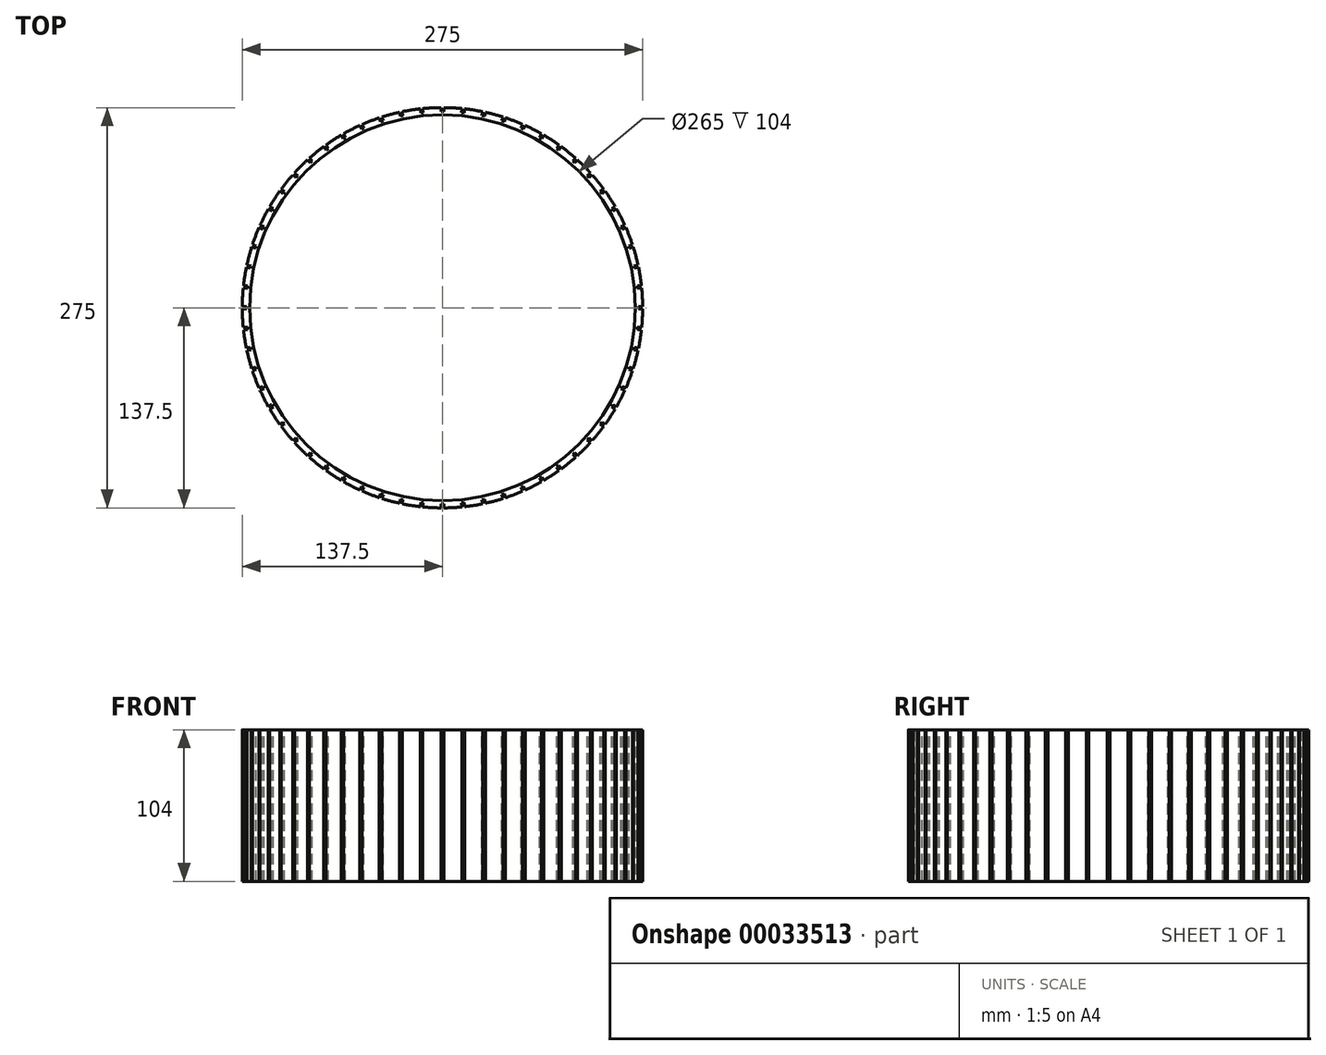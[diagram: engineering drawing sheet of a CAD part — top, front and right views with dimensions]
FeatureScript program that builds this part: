
annotation { "Feature Type Name" : "Feature", "Feature Type Description" : "" }
export const myFeature = defineFeature(function(context is Context, id is Id, definition is map)
    precondition{}
    {
        {
            var Q0;
            Q0=qCreatedBy(makeId("Top.planeOp"),FACE);
            var sketch = newSketch(context, id + "F0", { "sketchPlane" : qUnion([Q0])});
            skCircle(sketch, "E0", {"center": v(0, 0) * mm, "radius": 137.5 * mm});
            skCircle(sketch, "E1", {"center": v(0, 0) * mm, "radius": 132.5 * mm});
            skSolve(sketch);
        }
        {
            var Q0;
            Q0=makeQuery(id+"F0.imprint","IMPRINT",FACE,{"disambiguationData":[TD([[makeQuery(id+"F0.imprint","IMPRINT",EDGE,{"derivedFrom":sQuery(id+"F0.wireOp",EDGE,"E0")}),1.0]])]});
            extrude(context, id + "F1", {"entities" : qUnion([Q0]), "depth" : 104 * mm});
        }
        {
            var Q0;
            Q0=makeQuery(id+"F1.opExtrude","CAP_FACE",FACE,{"disambiguationData":[OSD([sQuery(id+"F0.wireOp",EDGE,"E0"),sQuery(id+"F0.wireOp",EDGE,"E1")])],"isStart":false});
            var sketch = newSketch(context, id + "F2", { "sketchPlane" : qUnion([Q0])});
            skCircle(sketch, "E2", {"center": v(0, 0) * mm, "radius": 134.7 * mm, "construction": true});
            skLineSegment(sketch, "E3", {"start": v(0, 0) * mm, "end": v(0, -137.5) * mm, "construction": true});
            skLineSegment(sketch, "E4.rect.bottom", {"start": v(0.9, -140.3) * mm, "end": v(-0.9, -140.3) * mm});
            skLineSegment(sketch, "E4.rect.top", {"start": v(0.9, -134.7) * mm, "end": v(-0.9, -134.7) * mm});
            skLineSegment(sketch, "E4.rect.left", {"start": v(0.9, -140.3) * mm, "end": v(0.9, -134.7) * mm});
            skLineSegment(sketch, "E4.rect.right", {"start": v(-0.9, -140.3) * mm, "end": v(-0.9, -134.7) * mm});
            skPoint(sketch, "E4.rect.middle", {"position": v(0, -137.5) * mm});
            skLineSegment(sketch, "E5.1.0", {"start": v(13.77, -139.63) * mm, "end": v(13.18, -134.06) * mm});
            skLineSegment(sketch, "E5.1.1", {"start": v(15.56, -139.44) * mm, "end": v(13.77, -139.63) * mm});
            skLineSegment(sketch, "E5.1.2", {"start": v(15.56, -139.44) * mm, "end": v(14.98, -133.87) * mm});
            skLineSegment(sketch, "E5.1.3", {"start": v(14.98, -133.87) * mm, "end": v(13.18, -134.06) * mm});
            skLineSegment(sketch, "E5.2.0", {"start": v(28.29, -137.42) * mm, "end": v(27.13, -131.94) * mm});
            skLineSegment(sketch, "E5.2.1", {"start": v(30.05, -137.05) * mm, "end": v(28.29, -137.42) * mm});
            skLineSegment(sketch, "E5.2.2", {"start": v(30.05, -137.05) * mm, "end": v(28.89, -131.57) * mm});
            skLineSegment(sketch, "E5.2.3", {"start": v(28.89, -131.57) * mm, "end": v(27.13, -131.94) * mm});
            skLineSegment(sketch, "E5.3.0", {"start": v(42.5, -133.71) * mm, "end": v(40.77, -128.39) * mm});
            skLineSegment(sketch, "E5.3.1", {"start": v(44.21, -133.16) * mm, "end": v(42.5, -133.71) * mm});
            skLineSegment(sketch, "E5.3.2", {"start": v(44.21, -133.16) * mm, "end": v(42.48, -127.83) * mm});
            skLineSegment(sketch, "E5.3.3", {"start": v(42.48, -127.83) * mm, "end": v(40.77, -128.39) * mm});
            skLineSegment(sketch, "E5.4.0", {"start": v(56.24, -128.54) * mm, "end": v(53.97, -123.42) * mm});
            skLineSegment(sketch, "E5.4.1", {"start": v(57.89, -127.8) * mm, "end": v(56.24, -128.54) * mm});
            skLineSegment(sketch, "E5.4.2", {"start": v(57.89, -127.8) * mm, "end": v(55.6, -122.69) * mm});
            skLineSegment(sketch, "E5.4.3", {"start": v(55.6, -122.69) * mm, "end": v(53.97, -123.42) * mm});
            skLineSegment(sketch, "E5.5.0", {"start": v(69.37, -121.95) * mm, "end": v(66.57, -117.1) * mm});
            skLineSegment(sketch, "E5.5.1", {"start": v(70.93, -121.05) * mm, "end": v(69.37, -121.95) * mm});
            skLineSegment(sketch, "E5.5.2", {"start": v(70.93, -121.05) * mm, "end": v(68.13, -116.2) * mm});
            skLineSegment(sketch, "E5.5.3", {"start": v(68.13, -116.2) * mm, "end": v(66.57, -117.1) * mm});
            skLineSegment(sketch, "E5.6.0", {"start": v(81.74, -114.03) * mm, "end": v(78.45, -109.5) * mm});
            skLineSegment(sketch, "E5.6.1", {"start": v(83.2, -112.98) * mm, "end": v(81.74, -114.03) * mm});
            skLineSegment(sketch, "E5.6.2", {"start": v(83.2, -112.98) * mm, "end": v(79.9, -108.45) * mm});
            skLineSegment(sketch, "E5.6.3", {"start": v(79.9, -108.45) * mm, "end": v(78.45, -109.5) * mm});
            skLineSegment(sketch, "E5.7.0", {"start": v(93.21, -104.87) * mm, "end": v(89.46, -100.7) * mm});
            skLineSegment(sketch, "E5.7.1", {"start": v(94.55, -103.66) * mm, "end": v(93.21, -104.87) * mm});
            skLineSegment(sketch, "E5.7.2", {"start": v(94.55, -103.66) * mm, "end": v(90.8, -99.5) * mm});
            skLineSegment(sketch, "E5.7.3", {"start": v(90.8, -99.5) * mm, "end": v(89.46, -100.7) * mm});
            skLineSegment(sketch, "E5.8.0", {"start": v(103.66, -94.55) * mm, "end": v(99.5, -90.8) * mm});
            skLineSegment(sketch, "E5.8.1", {"start": v(104.87, -93.21) * mm, "end": v(103.66, -94.55) * mm});
            skLineSegment(sketch, "E5.8.2", {"start": v(104.87, -93.21) * mm, "end": v(100.7, -89.46) * mm});
            skLineSegment(sketch, "E5.8.3", {"start": v(100.7, -89.46) * mm, "end": v(99.5, -90.8) * mm});
            skLineSegment(sketch, "E5.9.0", {"start": v(112.98, -83.2) * mm, "end": v(108.45, -79.9) * mm});
            skLineSegment(sketch, "E5.9.1", {"start": v(114.03, -81.74) * mm, "end": v(112.98, -83.2) * mm});
            skLineSegment(sketch, "E5.9.2", {"start": v(114.03, -81.74) * mm, "end": v(109.5, -78.45) * mm});
            skLineSegment(sketch, "E5.9.3", {"start": v(109.5, -78.45) * mm, "end": v(108.45, -79.9) * mm});
            skLineSegment(sketch, "E5.10.0", {"start": v(121.05, -70.93) * mm, "end": v(116.2, -68.13) * mm});
            skLineSegment(sketch, "E5.10.1", {"start": v(121.95, -69.37) * mm, "end": v(121.05, -70.93) * mm});
            skLineSegment(sketch, "E5.10.2", {"start": v(121.95, -69.37) * mm, "end": v(117.1, -66.57) * mm});
            skLineSegment(sketch, "E5.10.3", {"start": v(117.1, -66.57) * mm, "end": v(116.2, -68.13) * mm});
            skLineSegment(sketch, "E5.11.0", {"start": v(127.8, -57.89) * mm, "end": v(122.69, -55.6) * mm});
            skLineSegment(sketch, "E5.11.1", {"start": v(128.54, -56.24) * mm, "end": v(127.8, -57.89) * mm});
            skLineSegment(sketch, "E5.11.2", {"start": v(128.54, -56.24) * mm, "end": v(123.42, -53.97) * mm});
            skLineSegment(sketch, "E5.11.3", {"start": v(123.42, -53.97) * mm, "end": v(122.69, -55.6) * mm});
            skLineSegment(sketch, "E5.12.0", {"start": v(133.16, -44.21) * mm, "end": v(127.83, -42.48) * mm});
            skLineSegment(sketch, "E5.12.1", {"start": v(133.71, -42.5) * mm, "end": v(133.16, -44.21) * mm});
            skLineSegment(sketch, "E5.12.2", {"start": v(133.71, -42.5) * mm, "end": v(128.39, -40.77) * mm});
            skLineSegment(sketch, "E5.12.3", {"start": v(128.39, -40.77) * mm, "end": v(127.83, -42.48) * mm});
            skLineSegment(sketch, "E5.13.0", {"start": v(137.05, -30.05) * mm, "end": v(131.57, -28.89) * mm});
            skLineSegment(sketch, "E5.13.1", {"start": v(137.42, -28.29) * mm, "end": v(137.05, -30.05) * mm});
            skLineSegment(sketch, "E5.13.2", {"start": v(137.42, -28.29) * mm, "end": v(131.94, -27.13) * mm});
            skLineSegment(sketch, "E5.13.3", {"start": v(131.94, -27.13) * mm, "end": v(131.57, -28.89) * mm});
            skLineSegment(sketch, "E5.14.0", {"start": v(139.44, -15.56) * mm, "end": v(133.87, -14.98) * mm});
            skLineSegment(sketch, "E5.14.1", {"start": v(139.63, -13.77) * mm, "end": v(139.44, -15.56) * mm});
            skLineSegment(sketch, "E5.14.2", {"start": v(139.63, -13.77) * mm, "end": v(134.06, -13.18) * mm});
            skLineSegment(sketch, "E5.14.3", {"start": v(134.06, -13.18) * mm, "end": v(133.87, -14.98) * mm});
            skLineSegment(sketch, "E5.15.0", {"start": v(140.3, -0.9) * mm, "end": v(134.7, -0.9) * mm});
            skLineSegment(sketch, "E5.15.1", {"start": v(140.3, 0.9) * mm, "end": v(140.3, -0.9) * mm});
            skLineSegment(sketch, "E5.15.2", {"start": v(140.3, 0.9) * mm, "end": v(134.7, 0.9) * mm});
            skLineSegment(sketch, "E5.15.3", {"start": v(134.7, 0.9) * mm, "end": v(134.7, -0.9) * mm});
            skLineSegment(sketch, "E5.16.0", {"start": v(139.63, 13.77) * mm, "end": v(134.06, 13.18) * mm});
            skLineSegment(sketch, "E5.16.1", {"start": v(139.44, 15.56) * mm, "end": v(139.63, 13.77) * mm});
            skLineSegment(sketch, "E5.16.2", {"start": v(139.44, 15.56) * mm, "end": v(133.87, 14.98) * mm});
            skLineSegment(sketch, "E5.16.3", {"start": v(133.87, 14.98) * mm, "end": v(134.06, 13.18) * mm});
            skLineSegment(sketch, "E5.17.0", {"start": v(137.42, 28.29) * mm, "end": v(131.94, 27.13) * mm});
            skLineSegment(sketch, "E5.17.1", {"start": v(137.05, 30.05) * mm, "end": v(137.42, 28.29) * mm});
            skLineSegment(sketch, "E5.17.2", {"start": v(137.05, 30.05) * mm, "end": v(131.57, 28.89) * mm});
            skLineSegment(sketch, "E5.17.3", {"start": v(131.57, 28.89) * mm, "end": v(131.94, 27.13) * mm});
            skLineSegment(sketch, "E5.18.0", {"start": v(133.71, 42.5) * mm, "end": v(128.39, 40.77) * mm});
            skLineSegment(sketch, "E5.18.1", {"start": v(133.16, 44.21) * mm, "end": v(133.71, 42.5) * mm});
            skLineSegment(sketch, "E5.18.2", {"start": v(133.16, 44.21) * mm, "end": v(127.83, 42.48) * mm});
            skLineSegment(sketch, "E5.18.3", {"start": v(127.83, 42.48) * mm, "end": v(128.39, 40.77) * mm});
            skLineSegment(sketch, "E5.19.0", {"start": v(128.54, 56.24) * mm, "end": v(123.42, 53.97) * mm});
            skLineSegment(sketch, "E5.19.1", {"start": v(127.8, 57.89) * mm, "end": v(128.54, 56.24) * mm});
            skLineSegment(sketch, "E5.19.2", {"start": v(127.8, 57.89) * mm, "end": v(122.69, 55.6) * mm});
            skLineSegment(sketch, "E5.19.3", {"start": v(122.69, 55.6) * mm, "end": v(123.42, 53.97) * mm});
            skLineSegment(sketch, "E5.20.0", {"start": v(121.95, 69.37) * mm, "end": v(117.1, 66.57) * mm});
            skLineSegment(sketch, "E5.20.1", {"start": v(121.05, 70.93) * mm, "end": v(121.95, 69.37) * mm});
            skLineSegment(sketch, "E5.20.2", {"start": v(121.05, 70.93) * mm, "end": v(116.2, 68.13) * mm});
            skLineSegment(sketch, "E5.20.3", {"start": v(116.2, 68.13) * mm, "end": v(117.1, 66.57) * mm});
            skLineSegment(sketch, "E5.21.0", {"start": v(114.03, 81.74) * mm, "end": v(109.5, 78.45) * mm});
            skLineSegment(sketch, "E5.21.1", {"start": v(112.98, 83.2) * mm, "end": v(114.03, 81.74) * mm});
            skLineSegment(sketch, "E5.21.2", {"start": v(112.98, 83.2) * mm, "end": v(108.45, 79.9) * mm});
            skLineSegment(sketch, "E5.21.3", {"start": v(108.45, 79.9) * mm, "end": v(109.5, 78.45) * mm});
            skLineSegment(sketch, "E5.22.0", {"start": v(104.87, 93.21) * mm, "end": v(100.7, 89.46) * mm});
            skLineSegment(sketch, "E5.22.1", {"start": v(103.66, 94.55) * mm, "end": v(104.87, 93.21) * mm});
            skLineSegment(sketch, "E5.22.2", {"start": v(103.66, 94.55) * mm, "end": v(99.5, 90.8) * mm});
            skLineSegment(sketch, "E5.22.3", {"start": v(99.5, 90.8) * mm, "end": v(100.7, 89.46) * mm});
            skLineSegment(sketch, "E5.23.0", {"start": v(94.55, 103.66) * mm, "end": v(90.8, 99.5) * mm});
            skLineSegment(sketch, "E5.23.1", {"start": v(93.21, 104.87) * mm, "end": v(94.55, 103.66) * mm});
            skLineSegment(sketch, "E5.23.2", {"start": v(93.21, 104.87) * mm, "end": v(89.46, 100.7) * mm});
            skLineSegment(sketch, "E5.23.3", {"start": v(89.46, 100.7) * mm, "end": v(90.8, 99.5) * mm});
            skLineSegment(sketch, "E5.24.0", {"start": v(83.2, 112.98) * mm, "end": v(79.9, 108.45) * mm});
            skLineSegment(sketch, "E5.24.1", {"start": v(81.74, 114.03) * mm, "end": v(83.2, 112.98) * mm});
            skLineSegment(sketch, "E5.24.2", {"start": v(81.74, 114.03) * mm, "end": v(78.45, 109.5) * mm});
            skLineSegment(sketch, "E5.24.3", {"start": v(78.45, 109.5) * mm, "end": v(79.9, 108.45) * mm});
            skLineSegment(sketch, "E5.25.0", {"start": v(70.93, 121.05) * mm, "end": v(68.13, 116.2) * mm});
            skLineSegment(sketch, "E5.25.1", {"start": v(69.37, 121.95) * mm, "end": v(70.93, 121.05) * mm});
            skLineSegment(sketch, "E5.25.2", {"start": v(69.37, 121.95) * mm, "end": v(66.57, 117.1) * mm});
            skLineSegment(sketch, "E5.25.3", {"start": v(66.57, 117.1) * mm, "end": v(68.13, 116.2) * mm});
            skLineSegment(sketch, "E5.26.0", {"start": v(57.89, 127.8) * mm, "end": v(55.6, 122.69) * mm});
            skLineSegment(sketch, "E5.26.1", {"start": v(56.24, 128.54) * mm, "end": v(57.89, 127.8) * mm});
            skLineSegment(sketch, "E5.26.2", {"start": v(56.24, 128.54) * mm, "end": v(53.97, 123.42) * mm});
            skLineSegment(sketch, "E5.26.3", {"start": v(53.97, 123.42) * mm, "end": v(55.6, 122.69) * mm});
            skLineSegment(sketch, "E5.27.0", {"start": v(44.21, 133.16) * mm, "end": v(42.48, 127.83) * mm});
            skLineSegment(sketch, "E5.27.1", {"start": v(42.5, 133.71) * mm, "end": v(44.21, 133.16) * mm});
            skLineSegment(sketch, "E5.27.2", {"start": v(42.5, 133.71) * mm, "end": v(40.77, 128.39) * mm});
            skLineSegment(sketch, "E5.27.3", {"start": v(40.77, 128.39) * mm, "end": v(42.48, 127.83) * mm});
            skLineSegment(sketch, "E5.28.0", {"start": v(30.05, 137.05) * mm, "end": v(28.89, 131.57) * mm});
            skLineSegment(sketch, "E5.28.1", {"start": v(28.29, 137.42) * mm, "end": v(30.05, 137.05) * mm});
            skLineSegment(sketch, "E5.28.2", {"start": v(28.29, 137.42) * mm, "end": v(27.13, 131.94) * mm});
            skLineSegment(sketch, "E5.28.3", {"start": v(27.13, 131.94) * mm, "end": v(28.89, 131.57) * mm});
            skLineSegment(sketch, "E5.29.0", {"start": v(15.56, 139.44) * mm, "end": v(14.98, 133.87) * mm});
            skLineSegment(sketch, "E5.29.1", {"start": v(13.77, 139.63) * mm, "end": v(15.56, 139.44) * mm});
            skLineSegment(sketch, "E5.29.2", {"start": v(13.77, 139.63) * mm, "end": v(13.18, 134.06) * mm});
            skLineSegment(sketch, "E5.29.3", {"start": v(13.18, 134.06) * mm, "end": v(14.98, 133.87) * mm});
            skLineSegment(sketch, "E5.30.0", {"start": v(0.9, 140.3) * mm, "end": v(0.9, 134.7) * mm});
            skLineSegment(sketch, "E5.30.1", {"start": v(-0.9, 140.3) * mm, "end": v(0.9, 140.3) * mm});
            skLineSegment(sketch, "E5.30.2", {"start": v(-0.9, 140.3) * mm, "end": v(-0.9, 134.7) * mm});
            skLineSegment(sketch, "E5.30.3", {"start": v(-0.9, 134.7) * mm, "end": v(0.9, 134.7) * mm});
            skLineSegment(sketch, "E5.31.0", {"start": v(-13.77, 139.63) * mm, "end": v(-13.18, 134.06) * mm});
            skLineSegment(sketch, "E5.31.1", {"start": v(-15.56, 139.44) * mm, "end": v(-13.77, 139.63) * mm});
            skLineSegment(sketch, "E5.31.2", {"start": v(-15.56, 139.44) * mm, "end": v(-14.98, 133.87) * mm});
            skLineSegment(sketch, "E5.31.3", {"start": v(-14.98, 133.87) * mm, "end": v(-13.18, 134.06) * mm});
            skLineSegment(sketch, "E5.32.0", {"start": v(-28.29, 137.42) * mm, "end": v(-27.13, 131.94) * mm});
            skLineSegment(sketch, "E5.32.1", {"start": v(-30.05, 137.05) * mm, "end": v(-28.29, 137.42) * mm});
            skLineSegment(sketch, "E5.32.2", {"start": v(-30.05, 137.05) * mm, "end": v(-28.89, 131.57) * mm});
            skLineSegment(sketch, "E5.32.3", {"start": v(-28.89, 131.57) * mm, "end": v(-27.13, 131.94) * mm});
            skLineSegment(sketch, "E5.33.0", {"start": v(-42.5, 133.71) * mm, "end": v(-40.77, 128.39) * mm});
            skLineSegment(sketch, "E5.33.1", {"start": v(-44.21, 133.16) * mm, "end": v(-42.5, 133.71) * mm});
            skLineSegment(sketch, "E5.33.2", {"start": v(-44.21, 133.16) * mm, "end": v(-42.48, 127.83) * mm});
            skLineSegment(sketch, "E5.33.3", {"start": v(-42.48, 127.83) * mm, "end": v(-40.77, 128.39) * mm});
            skLineSegment(sketch, "E5.34.0", {"start": v(-56.24, 128.54) * mm, "end": v(-53.97, 123.42) * mm});
            skLineSegment(sketch, "E5.34.1", {"start": v(-57.89, 127.8) * mm, "end": v(-56.24, 128.54) * mm});
            skLineSegment(sketch, "E5.34.2", {"start": v(-57.89, 127.8) * mm, "end": v(-55.6, 122.69) * mm});
            skLineSegment(sketch, "E5.34.3", {"start": v(-55.6, 122.69) * mm, "end": v(-53.97, 123.42) * mm});
            skLineSegment(sketch, "E5.35.0", {"start": v(-69.37, 121.95) * mm, "end": v(-66.57, 117.1) * mm});
            skLineSegment(sketch, "E5.35.1", {"start": v(-70.93, 121.05) * mm, "end": v(-69.37, 121.95) * mm});
            skLineSegment(sketch, "E5.35.2", {"start": v(-70.93, 121.05) * mm, "end": v(-68.13, 116.2) * mm});
            skLineSegment(sketch, "E5.35.3", {"start": v(-68.13, 116.2) * mm, "end": v(-66.57, 117.1) * mm});
            skLineSegment(sketch, "E5.36.0", {"start": v(-81.74, 114.03) * mm, "end": v(-78.45, 109.5) * mm});
            skLineSegment(sketch, "E5.36.1", {"start": v(-83.2, 112.98) * mm, "end": v(-81.74, 114.03) * mm});
            skLineSegment(sketch, "E5.36.2", {"start": v(-83.2, 112.98) * mm, "end": v(-79.9, 108.45) * mm});
            skLineSegment(sketch, "E5.36.3", {"start": v(-79.9, 108.45) * mm, "end": v(-78.45, 109.5) * mm});
            skLineSegment(sketch, "E5.37.0", {"start": v(-93.21, 104.87) * mm, "end": v(-89.46, 100.7) * mm});
            skLineSegment(sketch, "E5.37.1", {"start": v(-94.55, 103.66) * mm, "end": v(-93.21, 104.87) * mm});
            skLineSegment(sketch, "E5.37.2", {"start": v(-94.55, 103.66) * mm, "end": v(-90.8, 99.5) * mm});
            skLineSegment(sketch, "E5.37.3", {"start": v(-90.8, 99.5) * mm, "end": v(-89.46, 100.7) * mm});
            skLineSegment(sketch, "E5.38.0", {"start": v(-103.66, 94.55) * mm, "end": v(-99.5, 90.8) * mm});
            skLineSegment(sketch, "E5.38.1", {"start": v(-104.87, 93.21) * mm, "end": v(-103.66, 94.55) * mm});
            skLineSegment(sketch, "E5.38.2", {"start": v(-104.87, 93.21) * mm, "end": v(-100.7, 89.46) * mm});
            skLineSegment(sketch, "E5.38.3", {"start": v(-100.7, 89.46) * mm, "end": v(-99.5, 90.8) * mm});
            skLineSegment(sketch, "E5.39.0", {"start": v(-112.98, 83.2) * mm, "end": v(-108.45, 79.9) * mm});
            skLineSegment(sketch, "E5.39.1", {"start": v(-114.03, 81.74) * mm, "end": v(-112.98, 83.2) * mm});
            skLineSegment(sketch, "E5.39.2", {"start": v(-114.03, 81.74) * mm, "end": v(-109.5, 78.45) * mm});
            skLineSegment(sketch, "E5.39.3", {"start": v(-109.5, 78.45) * mm, "end": v(-108.45, 79.9) * mm});
            skLineSegment(sketch, "E5.40.0", {"start": v(-121.05, 70.93) * mm, "end": v(-116.2, 68.13) * mm});
            skLineSegment(sketch, "E5.40.1", {"start": v(-121.95, 69.37) * mm, "end": v(-121.05, 70.93) * mm});
            skLineSegment(sketch, "E5.40.2", {"start": v(-121.95, 69.37) * mm, "end": v(-117.1, 66.57) * mm});
            skLineSegment(sketch, "E5.40.3", {"start": v(-117.1, 66.57) * mm, "end": v(-116.2, 68.13) * mm});
            skLineSegment(sketch, "E5.41.0", {"start": v(-127.8, 57.89) * mm, "end": v(-122.69, 55.6) * mm});
            skLineSegment(sketch, "E5.41.1", {"start": v(-128.54, 56.24) * mm, "end": v(-127.8, 57.89) * mm});
            skLineSegment(sketch, "E5.41.2", {"start": v(-128.54, 56.24) * mm, "end": v(-123.42, 53.97) * mm});
            skLineSegment(sketch, "E5.41.3", {"start": v(-123.42, 53.97) * mm, "end": v(-122.69, 55.6) * mm});
            skLineSegment(sketch, "E5.42.0", {"start": v(-133.16, 44.21) * mm, "end": v(-127.83, 42.48) * mm});
            skLineSegment(sketch, "E5.42.1", {"start": v(-133.71, 42.5) * mm, "end": v(-133.16, 44.21) * mm});
            skLineSegment(sketch, "E5.42.2", {"start": v(-133.71, 42.5) * mm, "end": v(-128.39, 40.77) * mm});
            skLineSegment(sketch, "E5.42.3", {"start": v(-128.39, 40.77) * mm, "end": v(-127.83, 42.48) * mm});
            skLineSegment(sketch, "E5.43.0", {"start": v(-137.05, 30.05) * mm, "end": v(-131.57, 28.89) * mm});
            skLineSegment(sketch, "E5.43.1", {"start": v(-137.42, 28.29) * mm, "end": v(-137.05, 30.05) * mm});
            skLineSegment(sketch, "E5.43.2", {"start": v(-137.42, 28.29) * mm, "end": v(-131.94, 27.13) * mm});
            skLineSegment(sketch, "E5.43.3", {"start": v(-131.94, 27.13) * mm, "end": v(-131.57, 28.89) * mm});
            skLineSegment(sketch, "E5.44.0", {"start": v(-139.44, 15.56) * mm, "end": v(-133.87, 14.98) * mm});
            skLineSegment(sketch, "E5.44.1", {"start": v(-139.63, 13.77) * mm, "end": v(-139.44, 15.56) * mm});
            skLineSegment(sketch, "E5.44.2", {"start": v(-139.63, 13.77) * mm, "end": v(-134.06, 13.18) * mm});
            skLineSegment(sketch, "E5.44.3", {"start": v(-134.06, 13.18) * mm, "end": v(-133.87, 14.98) * mm});
            skLineSegment(sketch, "E5.45.0", {"start": v(-140.3, 0.9) * mm, "end": v(-134.7, 0.9) * mm});
            skLineSegment(sketch, "E5.45.1", {"start": v(-140.3, -0.9) * mm, "end": v(-140.3, 0.9) * mm});
            skLineSegment(sketch, "E5.45.2", {"start": v(-140.3, -0.9) * mm, "end": v(-134.7, -0.9) * mm});
            skLineSegment(sketch, "E5.45.3", {"start": v(-134.7, -0.9) * mm, "end": v(-134.7, 0.9) * mm});
            skLineSegment(sketch, "E5.46.0", {"start": v(-139.63, -13.77) * mm, "end": v(-134.06, -13.18) * mm});
            skLineSegment(sketch, "E5.46.1", {"start": v(-139.44, -15.56) * mm, "end": v(-139.63, -13.77) * mm});
            skLineSegment(sketch, "E5.46.2", {"start": v(-139.44, -15.56) * mm, "end": v(-133.87, -14.98) * mm});
            skLineSegment(sketch, "E5.46.3", {"start": v(-133.87, -14.98) * mm, "end": v(-134.06, -13.18) * mm});
            skLineSegment(sketch, "E5.47.0", {"start": v(-137.42, -28.29) * mm, "end": v(-131.94, -27.13) * mm});
            skLineSegment(sketch, "E5.47.1", {"start": v(-137.05, -30.05) * mm, "end": v(-137.42, -28.29) * mm});
            skLineSegment(sketch, "E5.47.2", {"start": v(-137.05, -30.05) * mm, "end": v(-131.57, -28.89) * mm});
            skLineSegment(sketch, "E5.47.3", {"start": v(-131.57, -28.89) * mm, "end": v(-131.94, -27.13) * mm});
            skLineSegment(sketch, "E5.48.0", {"start": v(-133.71, -42.5) * mm, "end": v(-128.39, -40.77) * mm});
            skLineSegment(sketch, "E5.48.1", {"start": v(-133.16, -44.21) * mm, "end": v(-133.71, -42.5) * mm});
            skLineSegment(sketch, "E5.48.2", {"start": v(-133.16, -44.21) * mm, "end": v(-127.83, -42.48) * mm});
            skLineSegment(sketch, "E5.48.3", {"start": v(-127.83, -42.48) * mm, "end": v(-128.39, -40.77) * mm});
            skLineSegment(sketch, "E5.49.0", {"start": v(-128.54, -56.24) * mm, "end": v(-123.42, -53.97) * mm});
            skLineSegment(sketch, "E5.49.1", {"start": v(-127.8, -57.89) * mm, "end": v(-128.54, -56.24) * mm});
            skLineSegment(sketch, "E5.49.2", {"start": v(-127.8, -57.89) * mm, "end": v(-122.69, -55.6) * mm});
            skLineSegment(sketch, "E5.49.3", {"start": v(-122.69, -55.6) * mm, "end": v(-123.42, -53.97) * mm});
            skLineSegment(sketch, "E5.50.0", {"start": v(-121.95, -69.37) * mm, "end": v(-117.1, -66.57) * mm});
            skLineSegment(sketch, "E5.50.1", {"start": v(-121.05, -70.93) * mm, "end": v(-121.95, -69.37) * mm});
            skLineSegment(sketch, "E5.50.2", {"start": v(-121.05, -70.93) * mm, "end": v(-116.2, -68.13) * mm});
            skLineSegment(sketch, "E5.50.3", {"start": v(-116.2, -68.13) * mm, "end": v(-117.1, -66.57) * mm});
            skLineSegment(sketch, "E5.51.0", {"start": v(-114.03, -81.74) * mm, "end": v(-109.5, -78.45) * mm});
            skLineSegment(sketch, "E5.51.1", {"start": v(-112.98, -83.2) * mm, "end": v(-114.03, -81.74) * mm});
            skLineSegment(sketch, "E5.51.2", {"start": v(-112.98, -83.2) * mm, "end": v(-108.45, -79.9) * mm});
            skLineSegment(sketch, "E5.51.3", {"start": v(-108.45, -79.9) * mm, "end": v(-109.5, -78.45) * mm});
            skLineSegment(sketch, "E5.52.0", {"start": v(-104.87, -93.21) * mm, "end": v(-100.7, -89.46) * mm});
            skLineSegment(sketch, "E5.52.1", {"start": v(-103.66, -94.55) * mm, "end": v(-104.87, -93.21) * mm});
            skLineSegment(sketch, "E5.52.2", {"start": v(-103.66, -94.55) * mm, "end": v(-99.5, -90.8) * mm});
            skLineSegment(sketch, "E5.52.3", {"start": v(-99.5, -90.8) * mm, "end": v(-100.7, -89.46) * mm});
            skLineSegment(sketch, "E5.53.0", {"start": v(-94.55, -103.66) * mm, "end": v(-90.8, -99.5) * mm});
            skLineSegment(sketch, "E5.53.1", {"start": v(-93.21, -104.87) * mm, "end": v(-94.55, -103.66) * mm});
            skLineSegment(sketch, "E5.53.2", {"start": v(-93.21, -104.87) * mm, "end": v(-89.46, -100.7) * mm});
            skLineSegment(sketch, "E5.53.3", {"start": v(-89.46, -100.7) * mm, "end": v(-90.8, -99.5) * mm});
            skLineSegment(sketch, "E5.54.0", {"start": v(-83.2, -112.98) * mm, "end": v(-79.9, -108.45) * mm});
            skLineSegment(sketch, "E5.54.1", {"start": v(-81.74, -114.03) * mm, "end": v(-83.2, -112.98) * mm});
            skLineSegment(sketch, "E5.54.2", {"start": v(-81.74, -114.03) * mm, "end": v(-78.45, -109.5) * mm});
            skLineSegment(sketch, "E5.54.3", {"start": v(-78.45, -109.5) * mm, "end": v(-79.9, -108.45) * mm});
            skLineSegment(sketch, "E5.55.0", {"start": v(-70.93, -121.05) * mm, "end": v(-68.13, -116.2) * mm});
            skLineSegment(sketch, "E5.55.1", {"start": v(-69.37, -121.95) * mm, "end": v(-70.93, -121.05) * mm});
            skLineSegment(sketch, "E5.55.2", {"start": v(-69.37, -121.95) * mm, "end": v(-66.57, -117.1) * mm});
            skLineSegment(sketch, "E5.55.3", {"start": v(-66.57, -117.1) * mm, "end": v(-68.13, -116.2) * mm});
            skLineSegment(sketch, "E5.56.0", {"start": v(-57.89, -127.8) * mm, "end": v(-55.6, -122.69) * mm});
            skLineSegment(sketch, "E5.56.1", {"start": v(-56.24, -128.54) * mm, "end": v(-57.89, -127.8) * mm});
            skLineSegment(sketch, "E5.56.2", {"start": v(-56.24, -128.54) * mm, "end": v(-53.97, -123.42) * mm});
            skLineSegment(sketch, "E5.56.3", {"start": v(-53.97, -123.42) * mm, "end": v(-55.6, -122.69) * mm});
            skLineSegment(sketch, "E5.57.0", {"start": v(-44.21, -133.16) * mm, "end": v(-42.48, -127.83) * mm});
            skLineSegment(sketch, "E5.57.1", {"start": v(-42.5, -133.71) * mm, "end": v(-44.21, -133.16) * mm});
            skLineSegment(sketch, "E5.57.2", {"start": v(-42.5, -133.71) * mm, "end": v(-40.77, -128.39) * mm});
            skLineSegment(sketch, "E5.57.3", {"start": v(-40.77, -128.39) * mm, "end": v(-42.48, -127.83) * mm});
            skLineSegment(sketch, "E5.58.0", {"start": v(-30.05, -137.05) * mm, "end": v(-28.89, -131.57) * mm});
            skLineSegment(sketch, "E5.58.1", {"start": v(-28.29, -137.42) * mm, "end": v(-30.05, -137.05) * mm});
            skLineSegment(sketch, "E5.58.2", {"start": v(-28.29, -137.42) * mm, "end": v(-27.13, -131.94) * mm});
            skLineSegment(sketch, "E5.58.3", {"start": v(-27.13, -131.94) * mm, "end": v(-28.89, -131.57) * mm});
            skLineSegment(sketch, "E5.59.0", {"start": v(-15.56, -139.44) * mm, "end": v(-14.98, -133.87) * mm});
            skLineSegment(sketch, "E5.59.1", {"start": v(-13.77, -139.63) * mm, "end": v(-15.56, -139.44) * mm});
            skLineSegment(sketch, "E5.59.2", {"start": v(-13.77, -139.63) * mm, "end": v(-13.18, -134.06) * mm});
            skLineSegment(sketch, "E5.59.3", {"start": v(-13.18, -134.06) * mm, "end": v(-14.98, -133.87) * mm});
            skSolve(sketch);
        }
        {
            var Q0;
            Q0 = qSketchRegion(id + "F2", true);
            extrude(context, id + "F3", {"entities" : qUnion([Q0]), "operationType" : NewBodyOperationType.REMOVE, "endBound" : BoundingType.THROUGH_ALL, "oppositeDirection" : true, "depth" : 25 * mm});
        }
    });
